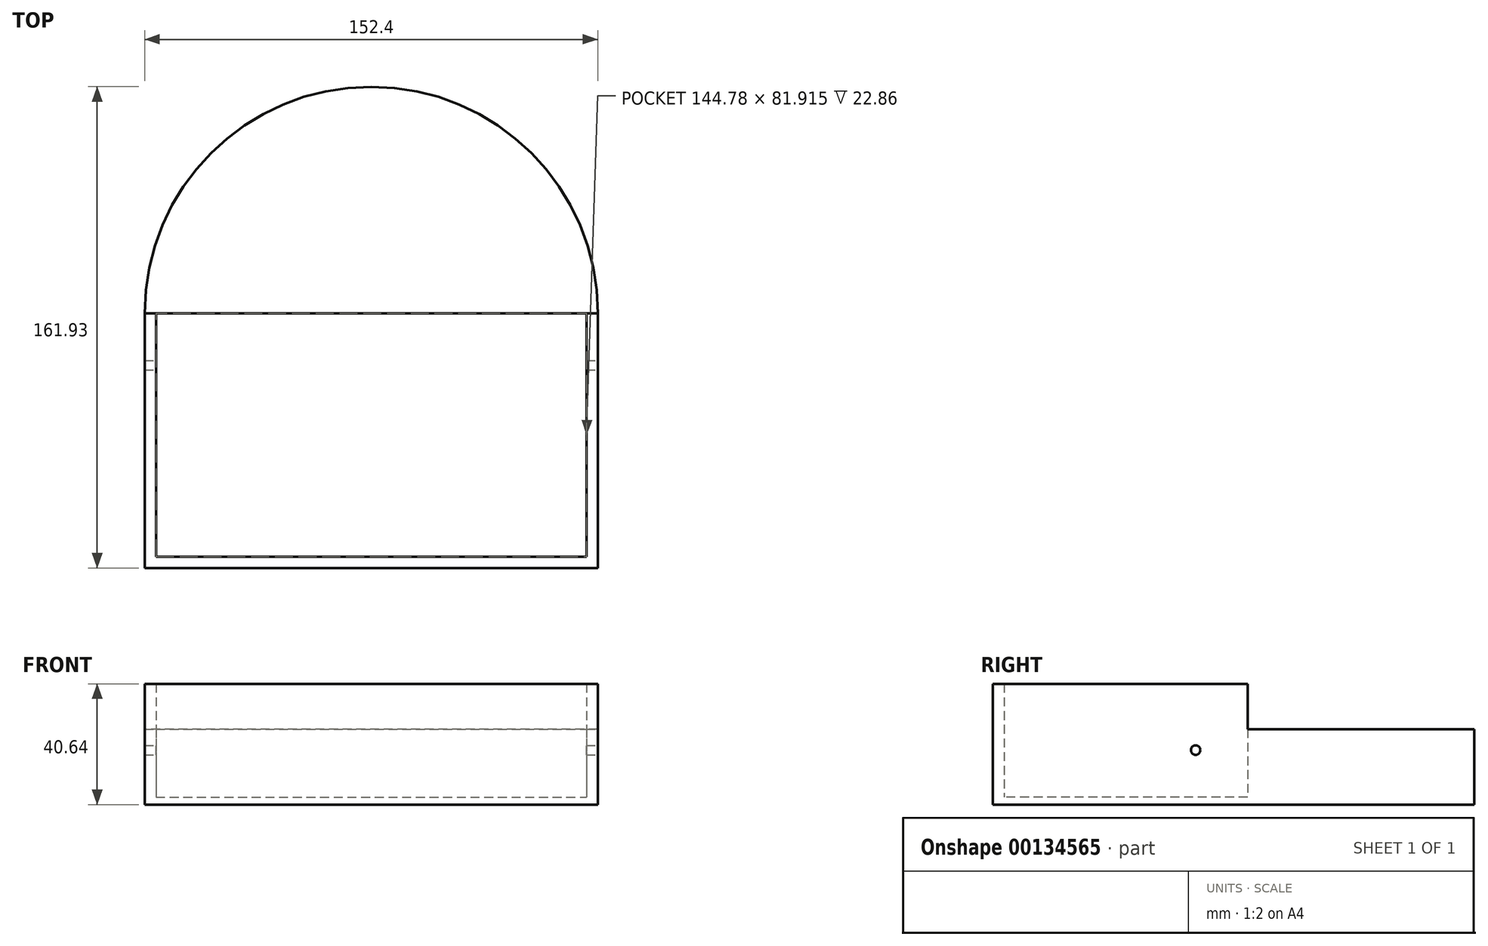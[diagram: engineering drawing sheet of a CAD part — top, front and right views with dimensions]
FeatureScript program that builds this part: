
annotation { "Feature Type Name" : "Feature", "Feature Type Description" : "" }
export const myFeature = defineFeature(function(context is Context, id is Id, definition is map)
    precondition{}
    {
        {
            var Q0;
            Q0=qCreatedBy(makeId("Top.planeOp"),FACE);
            var sketch = newSketch(context, id + "F0", { "sketchPlane" : qUnion([Q0])});
            skLineSegment(sketch, "E0.bottom", {"start": v(0, 0) * mm, "end": v(-152.4, 0) * mm});
            skLineSegment(sketch, "E0.top", {"start": v(0, 85.73) * mm, "end": v(-152.4, 85.73) * mm});
            skLineSegment(sketch, "E0.left", {"start": v(0, 0) * mm, "end": v(0, 85.73) * mm});
            skLineSegment(sketch, "E0.right", {"start": v(-152.4, 0) * mm, "end": v(-152.4, 85.72) * mm});
            skPoint(sketch, "E1", {"position": v(-76.2, 85.73) * mm});
            skCircle(sketch, "E2", {"center": v(-76.2, 85.73) * mm, "radius": 76.2 * mm});
            skSolve(sketch);
        }
        {
            var Q0;
            Q0 = qSketchRegion(id + "F0", true);
            extrude(context, id + "F1", {"entities" : qUnion([Q0]), "depth" : 2.54 * mm});
        }
        {
            var Q0;
            Q0=makeQuery(id+"F1.opExtrude","CAP_FACE",FACE,{"disambiguationData":[OSD([sQuery(id+"F0.wireOp",EDGE,"E0.bottom"),sQuery(id+"F0.wireOp",EDGE,"E0.left"),sQuery(id+"F0.wireOp",EDGE,"E0.right"),sQuery(id+"F0.wireOp",EDGE,"E2")])],"isStart":false});
            var sketch = newSketch(context, id + "F2", { "sketchPlane" : qUnion([Q0])});
            skPoint(sketch, "E3", {"position": v(-76.2, 85.73) * mm});
            skArc(sketch, "E4", {"start": v(0, 85.73) * mm, "mid": v(-76.2, 161.93) * mm, "end": v(-152.4, 85.73) * mm});
            skPoint(sketch, "E5", {"position": v(-152.4, 85.72) * mm});
            skPoint(sketch, "E6", {"position": v(0, 85.73) * mm});
            skLineSegment(sketch, "E7", {"start": v(-152.4, 85.73) * mm, "end": v(0, 85.73) * mm});
            skSolve(sketch);
        }
        {
            var Q0;
            Q0 = qSketchRegion(id + "F2", true);
            extrude(context, id + "F3", {"entities" : qUnion([Q0]), "operationType" : NewBodyOperationType.ADD, "depth" : 22.86 * mm});
        }
        {
            var Q0;
            Q0=makeQuery(id+"F1.opExtrude","CAP_FACE",FACE,{"disambiguationData":[OSD([sQuery(id+"F0.wireOp",EDGE,"E0.bottom"),sQuery(id+"F0.wireOp",EDGE,"E0.left"),sQuery(id+"F0.wireOp",EDGE,"E0.right"),sQuery(id+"F0.wireOp",EDGE,"E2")])],"isStart":false});
            var sketch = newSketch(context, id + "F4", { "sketchPlane" : qUnion([Q0])});
            skLineSegment(sketch, "E8.top", {"start": v(-148.6, 3.8) * mm, "end": v(-3.8, 3.81) * mm});
            skLineSegment(sketch, "E8.left", {"start": v(-148.6, 85.73) * mm, "end": v(-148.6, 3.8) * mm});
            skLineSegment(sketch, "E8.right", {"start": v(-3.81, 85.73) * mm, "end": v(-3.8, 3.81) * mm});
            skLineSegment(sketch, "E9", {"start": v(-3.81, 85.73) * mm, "end": v(0, 85.73) * mm});
            skLineSegment(sketch, "E10", {"start": v(0, 85.73) * mm, "end": v(0, 0) * mm});
            skLineSegment(sketch, "E11", {"start": v(-152.4, 0) * mm, "end": v(0, 0) * mm});
            skLineSegment(sketch, "E12", {"start": v(-152.4, 0) * mm, "end": v(-152.4, 85.72) * mm});
            skLineSegment(sketch, "E13", {"start": v(-152.4, 85.73) * mm, "end": v(-148.6, 85.73) * mm});
            skSolve(sketch);
        }
        {
            var Q0;
            Q0 = qSketchRegion(id + "F4", true);
            extrude(context, id + "F5", {"entities" : qUnion([Q0]), "operationType" : NewBodyOperationType.ADD, "depth" : 38.1 * mm});
        }
        {
            var Q0;
            Q0=makeQuery(id+"F5.boolean.opBoolean","MERGE",FACE,{"derivedFrom":[makeQuery(id+"F1.opExtrude","SWEPT_FACE",FACE,{"disambiguationData":[OSD([sQuery(id+"F0.wireOp",EDGE,"E0.right")])]}),makeQuery(id+"F5.opExtrude","SWEPT_FACE",FACE,{"disambiguationData":[OSD([sQuery(id+"F4.wireOp",EDGE,"E12")])]})]});
            var sketch = newSketch(context, id + "F6", { "sketchPlane" : qUnion([Q0])});
            skCircle(sketch, "E14", {"center": v(-68.2, 18.33) * mm, "radius": 1.59 * mm});
            skSolve(sketch);
        }
        {
            var Q0;
            Q0 = qSketchRegion(id + "F6", true);
            extrude(context, id + "F7", {"entities" : qUnion([Q0]), "operationType" : NewBodyOperationType.REMOVE, "endBound" : BoundingType.SYMMETRIC, "depth" : 508 * mm});
        }
    });
